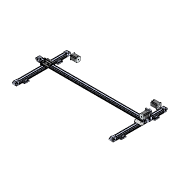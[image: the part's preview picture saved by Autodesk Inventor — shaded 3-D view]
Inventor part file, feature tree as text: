
AUTODESK INVENTOR PART (.ipt)
format: ipt  version: 2020 (Build 240168000, 168)  size: 19,587,072 bytes
history: native  units: mm
features: other x48, sketch x3, projected_geometry x3, extrude x2, hole x1, chamfer x1, fillet x1
ambient origin geometry x8: Origin, YZ Plane, XZ Plane, XY Plane, X Axis, Y Axis, Z Axis, Center Point
bodies: Body1 (feature_tree), Body2 (feature_tree), Body3 (feature_tree), Body4 (feature_tree), Body5 (feature_tree), Body6 (feature_tree), Body7 (feature_tree), Body8 (feature_tree), Body9 (feature_tree), Body10 (feature_tree), Body11 (feature_tree), Body12 (feature_tree), Body13 (feature_tree), Body14 (feature_tree), Body15 (feature_tree), Body16 (feature_tree), Body17 (feature_tree), Body18 (feature_tree), Body19 (feature_tree), Body20 (feature_tree), Body21 (feature_tree), Body22 (feature_tree), Body23 (feature_tree), Body24 (feature_tree)
feature tree (59):
  other  "CCM_Unit.iam"
  other  "CCM_Unit_C.iam:1::RAIL W40-06_B.ipt:1"
  other  "CCM_Unit_C.iam:1::TAILSTOCK W40-00_0+0.ipt:1"
  other  "CCM_Unit_C.iam:1::CART HK32-06W-00__1.ipt:1"
  other  "CCM_Unit_C.iam:1::TAILSTOCK W40-00_0+22_1.ipt:1"
  other  "CCM_Unit_A.iam:1::RAIL W40-06.ipt:1"
  other  "CCM_Unit_A.iam:1::TAILSTOCK W40-00_0+0.ipt:1"
  other  "CCM_Unit_A.iam:1::TAILSTOCK W40-00_22+0_1.ipt:1"
  other  "CCM_Unit_A.iam:1::CART HK32-06W-00__1.ipt:1"
  other  "CCM_Unit_A.iam:1::40 RAIL MOUNT__1.ipt:1"
  other  "CCM_Unit_A.iam:1::40 RAIL MOUNT__1.ipt:2"
  other  "CCM_Unit_B.iam:1::RAIL W40-06.ipt:1"
  other  "CCM_Unit_B.iam:1::TAILSTOCK W40-00_0+0.ipt:1"
  other  "CCM_Unit_B.iam:1::CART HK32-06W-00__1.ipt:1"
  other  "CCM_Unit_B.iam:1::TAILSTOCK W40-00_0+22_1.ipt:1"
  other  "CCM_Unit_B.iam:1::40 RAIL MOUNT__1.ipt:1"
  other  "CCM_Unit_B.iam:1::40 RAIL MOUNT__1.ipt:2"
  other  "CCM_Mount_A.ipt:2"
  other  "57 Aside Speed Reducer(2050)__1.ipt:1"
  other  "NEMA23 Stepper.ipt:1"
  other  "NEMA23 Stepper.ipt:2"
  other  "NEMA23 Stepper.ipt:3"
  other  "CCM_Mount_B.ipt:1"
  other  "OMRON SS-5GL .ipt:1"
  other  "ソリッド1"
  extrude  "押し出し1"  Depth=10.0mm
  hole  "穴1"  [1 undecoded]
  chamfer  "面取り1"  Distance=25.0mm
  extrude  "押し出し2"  Depth=10.0mm TaperAngle=0.0deg
  fillet  "フィレット1"  Radius=2.7mm
  other  "ソリッド2"
  other  "ソリッド3"
  other  "ソリッド4"
  other  "ソリッド5"
  other  "ソリッド6"
  other  "ソリッド7"
  other  "ソリッド8"
  other  "ソリッド9"
  other  "ソリッド10"
  other  "ソリッド11"
  other  "ソリッド12"
  other  "ソリッド13"
  other  "ソリッド14"
  other  "ソリッド15"
  other  "ソリッド16"
  other  "ソリッド17"
  other  "ソリッド18"
  other  "ソリッド19"
  other  "ソリッド20"
  other  "ソリッド21"
  other  "ソリッド22"
  other  "ソリッド25"
  sketch  "スケッチ1"
  projected_geometry  "投影ループ1"
  other  "ソリッド26"
  sketch  "スケッチ2"
  projected_geometry  "投影ループ2"
  sketch  "スケッチ3"
  projected_geometry  "投影ループ3"
note: 1 required parameter value undecoded (feature->parameter linkage not recoverable at this tier; creation-order binding heuristic only, values carry confidence <= 0.55)
